# Revit family: DF_ДержательИзолированногоМолниеприемника_8-10_72918_EZETEK
name_source: partatom
category: Соединительные детали воздуховодов
revit_build: Autodesk Revit 2017 (Build: 20170118_1100(x64)
units: mm (PartAtom-declared; Revit-internal decimal feet)

## family parameters
Всегда вертикально = Да
На основе рабочей плоскости = Нет
Общий = Нет
При загрузке вырезать с полостями = Нет
Размер круглого соединителя = Использовать радиус
Тип детали = Соединение

## types (1)
- ДержательПроводникаКруглогоДляКонька_6-10_91107
    ADSK_Версия Revit = 2017
    ADSK_Единица измерения = Неспецифицируемое
    ADSK_Завод-изготовитель = Неспецифицируемое
    ADSK_Код изделия = Неспецифицируемое
    ADSK_Количество = 0
    ADSK_Марка = Неспецифицируемое
    ADSK_Масса = 0
    ADSK_Масса_Текст = Неспецифицируемое
    ADSK_Материал = BIMLIB_Сталь_Оцинкованная_EZETEK
    ADSK_Наименование = Неспецифицируемое
    ADSK_Обозначение = Неспецифицируемое
    URL = https://ezetek.ru
    Группа модели = Изолированная молниезащита
    Изготовитель = Ezetek
    Описание = Изоляционная штанга для монтажа молниеприемных токоотводов и других проводников с соблюдением разделительного интервала (интервал разделения = 750 мм). Изготовлен из стеклопластика, армированного стекловолокном. Используется для фиксации к стене, опоре, или мачте молниеприемника. Фиксация к стене осуществляется с помощью опоры мостовой с крепежными отверстиями 8,4. Для фиксации к опоре, или мачте с помощью болтового окончания и гайки М8  используется корнштейн трубный, или опора на ленту.
    Тип = FA_ДержательИзолированногоМолниеприемника_8-10_91107_EZETEK : ДержательПроводникаКруглогоДляКонька_6-10_91107
    Угол = 90.00°
